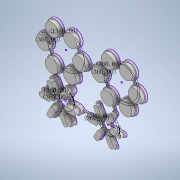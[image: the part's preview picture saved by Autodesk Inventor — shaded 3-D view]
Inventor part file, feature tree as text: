
AUTODESK INVENTOR PART (.ipt)
format: ipt  version: 2022 (Build 260153000, 153)  size: 585,216 bytes
history: native  units: mm
features: extrude x7, sketch x1
ambient origin geometry x8: Origin, YZ Plane, XZ Plane, XY Plane, X Axis, Y Axis, Z Axis, Center Point
bodies: 实体1 (feature_tree)
feature tree (8):
  sketch  "草图1"  dims[d2=3.0mm d3=3.0mm d4=2.0mm d5=3.0mm d7=9.5mm d8=8.0mm d16=60.0mm d18=60.0mm d27=3.0mm d28=2.0mm d29=3.0mm d30=9.0mm d31=5.0mm d32=360.0deg d33=360.0deg d44=60.0mm d46=360.0deg d49=60.0mm d51=360.0deg d54=60.0mm d56=60.0mm d58=60.0mm d60=60.0mm d61=9.5mm d62=8.0mm d63=360.0deg d64=360.0deg d65=60.0mm d67=360.0deg d69=60.0mm d71=360.0deg d73=1.2mm d74=0.0mm d75=3.2mm d76=0.0mm d77=2.2mm d78=0.0mm d79=4.7mm d80=0.0mm d81=2.8mm d82=0.0mm d83=1.0mm d84=0.0mm d85=0.8mm d86=0.0mm]
  extrude  "拉伸1"  Depth=0.8mm
  extrude  "拉伸2"  Depth=0.8mm TaperAngle=360.0deg
  extrude  "拉伸3"  Depth=0.8mm TaperAngle=360.0deg
  extrude  "拉伸4"  Depth=0.8mm TaperAngle=360.0deg
  extrude  "拉伸5"  Depth=0.8mm TaperAngle=360.0deg
  extrude  "拉伸6"  Depth=1.2mm TaperAngle=0.0deg
  extrude  "拉伸7"  Depth=3.2mm TaperAngle=0.0deg
